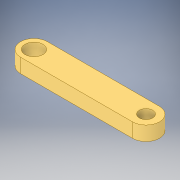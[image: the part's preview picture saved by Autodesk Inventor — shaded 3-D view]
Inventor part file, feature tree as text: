
AUTODESK INVENTOR PART (.ipt)
format: ipt  version: 2019 (Build 230136000, 136)  size: 118,272 bytes
history: native  units: mm
features: other x1, extrude x1, sketch x1
ambient origin geometry x8: Origin, YZ Plane, XZ Plane, XY Plane, X Axis, Y Axis, Z Axis, Center Point
bodies: Body1 (feature_tree)
feature tree (3):
  other  "Sólido1"
  extrude  "Extrusión1"  Depth=6.0mm
  sketch  "Boceto1"  dims[d0=25.0mm d1=6.0mm d2=4.0mm d3=3.0mm d4=3.18mm d5=0.0mm]
